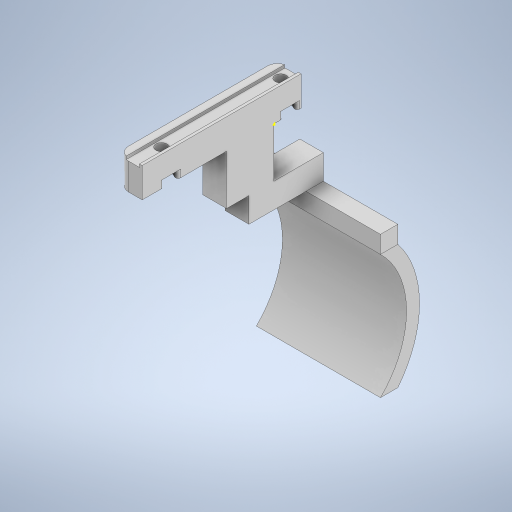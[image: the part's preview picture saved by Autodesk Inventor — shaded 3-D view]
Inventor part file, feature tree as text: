
AUTODESK INVENTOR PART (.ipt)
format: ipt  version: 2024 (Build 280153000, 153)  size: 372,224 bytes
history: native  units: in
note: dims shown in document units (in); Inventor stores cm internally (conversion verified against a paired STEP export)
features: sketch x10, extrude x7, projected_geometry x4, fillet x2, sweep x1
ambient origin geometry x8: Origin, YZ Plane, XZ Plane, XY Plane, X Axis, Y Axis, Z Axis, Center Point
bodies: Solid1 (feature_tree), Solid2 (feature_tree)
feature tree (24):
  extrude  "Extrusion1"  Depth=2.5197in
  extrude  "Extrusion2"  Depth=1.8898in
  extrude  "Extrusion3"  Depth=0.4724in TaperAngle=0.0deg
  fillet  "Fillet1"  Radius=0.0433in
  fillet  "Fillet2"  Radius=0.2126in
  extrude  "Extrusion19"  Depth=0.4724in TaperAngle=0.0deg
  extrude  "Extrusion21"  Depth=0.1181in TaperAngle=0.0deg
  sketch  "Sketch41"  dims[d17=0.1772in d18=0.0394in]
  extrude  "Extrusion22"  Depth=0.0394in
  sweep  "Sweep4"
  extrude  "Extrusion24"  Depth=0.748in
  sketch  "Sketch1"  dims[d1=0.374in d2=2.5197in]
  sketch  "Sketch2"  dims[d3=0.1772in d4=1.8898in]
  sketch  "Sketch3"  dims[d6=0.1457in d7=0.4724in d8=0.0in d9=0.0433in d10=0.2126in]
  projected_geometry  "Projected Loop2"
  projected_geometry  "Projected Loop3"
  projected_geometry  "Projected Loop4"
  projected_geometry  "Projected Loop5"
  sketch  "Sketch28"  dims[d11=0.0472in d12=0.4724in d13=0.0in]
  sketch  "Sketch40"  dims[d14=0.2953in d15=0.1181in d16=0.0in]
  sketch  "Sketch42"  dims[d19=0.1575in d76=0.4724in]
  sketch  "Sketch50"  dims[d107=0.102in d108=0.748in]
  sketch  "Sketch51"  dims[d109=0.7874in d110=0.0in]
  sketch  "Sketch57"  dims[d130=0.7874in d131=1.1811in d132=0.3937in d133=0.0in d134=1.1811in d135=0.2756in d137=1.9685in d138=0.2756in d139=0.0in d147=1.9685in d148=1.378in d149=0.0in d150=0.0in d154=3.8563in d155=0.0in d42=0.0197in d43=0.0344in d44=0.0197in d45=0.0344in d46=0.0in d47=0.0in d48=0.0in d49=0.0in d50=0.0in d51=0.0in d52=0.0in d53=0.0in d55=0.0197in d56=0.0344in d57=0.0197in d58=0.0344in d60=0.0197in d61=0.0344in d62=0.0197in d63=0.0344in d72=0.0197in d73=0.0344in d74=0.0197in d75=0.0344in d140=0.0197in d141=0.0344in]
